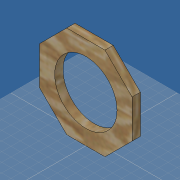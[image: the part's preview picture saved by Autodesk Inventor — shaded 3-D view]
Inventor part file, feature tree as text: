
AUTODESK INVENTOR PART (.ipt)
format: ipt  version: 2019 (Build 230136000, 136)  size: 116,736 bytes
history: native  units: mm
features: other x1, extrude x1, sketch x1
ambient origin geometry x8: Origin, YZ Plane, XZ Plane, XY Plane, X Axis, Y Axis, Z Axis, Center Point
bodies: Body1 (feature_tree)
feature tree (3):
  other  "<userpath>\OneDrive\Dokumente\Inventor\Absauganlage\Absauganlage_Params.xlsx"
  extrude  "Extrusion2"  Depth=18.0mm TaperAngle=0.0deg
  sketch  "Skizze2"  dims[d7=135.0mm d8=18.0mm d9=0.0mm d11=200.0mm]
